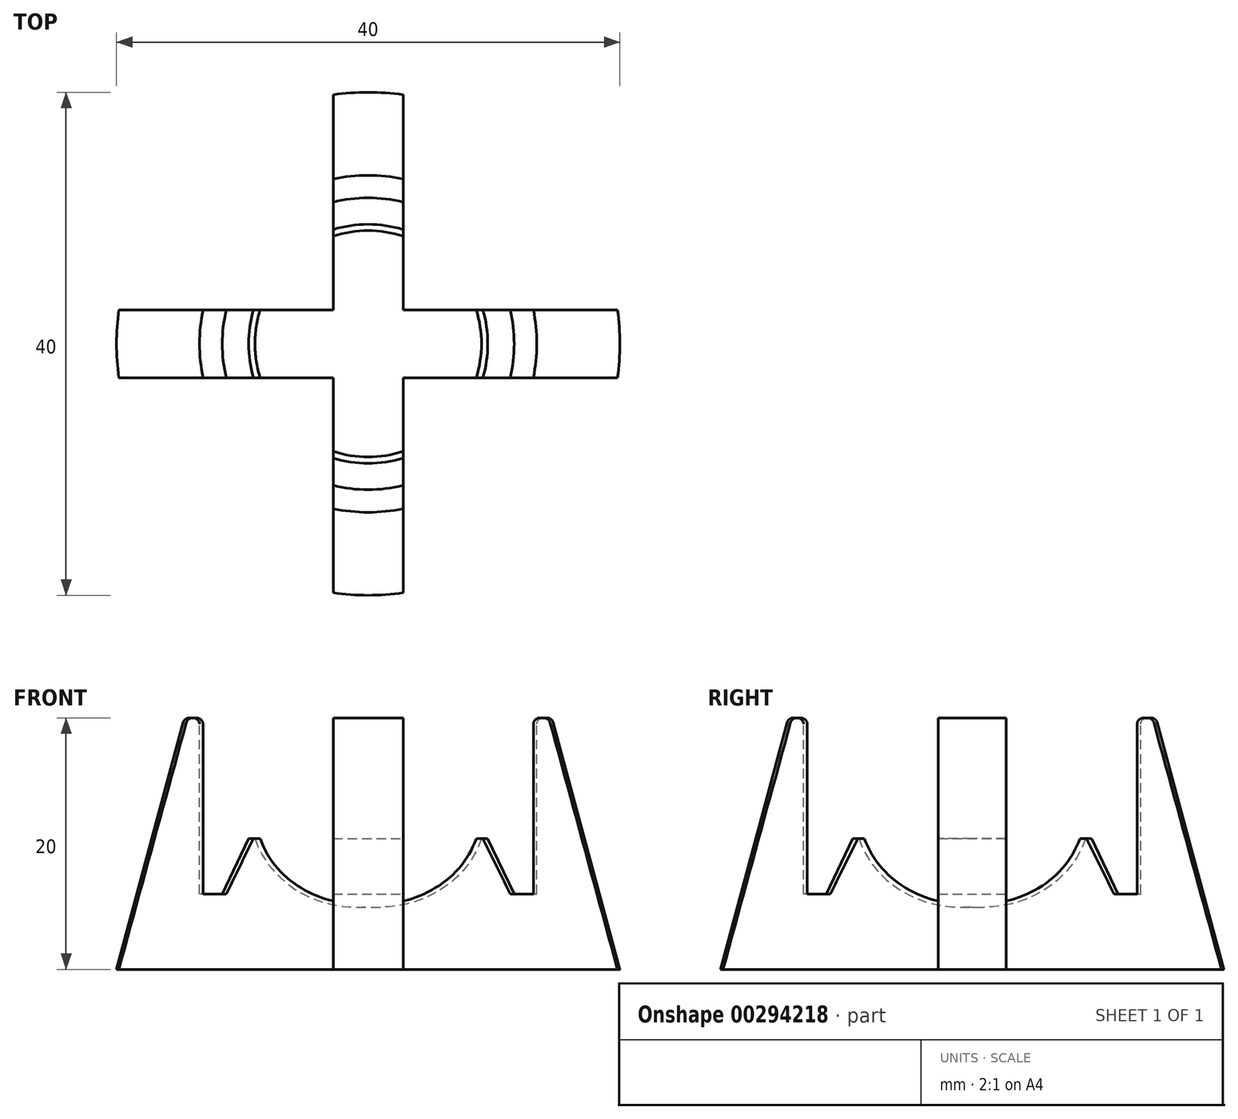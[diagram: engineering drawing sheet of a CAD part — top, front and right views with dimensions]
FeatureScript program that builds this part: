
annotation { "Feature Type Name" : "Feature", "Feature Type Description" : "" }
export const myFeature = defineFeature(function(context is Context, id is Id, definition is map)
    precondition{}
    {
        {
            var Q0;
            Q0=qCreatedBy(makeId("Front.planeOp"),FACE);
            var sketch = newSketch(context, id + "F0", { "sketchPlane" : qUnion([Q0])});
            skLineSegment(sketch, "E0", {"start": v(0, 0) * mm, "end": v(-20, 0) * mm});
            skLineSegment(sketch, "E1", {"start": v(-20, 0) * mm, "end": v(-14.6, 20) * mm});
            skLineSegment(sketch, "E2", {"start": v(-14.6, 20) * mm, "end": v(-13.4, 20) * mm});
            skLineSegment(sketch, "E3", {"start": v(-13.4, 20) * mm, "end": v(-13.4, 20) * mm});
            skLineSegment(sketch, "E4", {"start": v(0, 5) * mm, "end": v(0, 0) * mm});
            skPoint(sketch, "E5", {"position": v(-9.5, 10.4) * mm});
            skLineSegment(sketch, "E6", {"start": v(-9.5, 10.4) * mm, "end": v(-11.6, 6) * mm});
            skLineSegment(sketch, "E7", {"start": v(-13.4, 20) * mm, "end": v(-13.4, 6) * mm});
            skLineSegment(sketch, "E8", {"start": v(-13.4, 6) * mm, "end": v(-11.6, 6) * mm});
            skLineSegment(sketch, "E9", {"start": v(-9.5, 10.4) * mm, "end": v(-9, 10.4) * mm});
            skEllipticalArc(sketch, "E10", {});
            skPoint(sketch, "E11", {"position": v(-13.4, 12.7) * mm});
            const initialGuessF0  = {"E10": [-0.0009394245789034281, 0.012652029710676027, 0, -1, 0.0077, 0.00842914595487551, 5.0091991960001465, 0.11168157500112041]};
            skSetInitialGuess(sketch, initialGuessF0);
            skSolve(sketch);
        }
        {
            var Q0;
            Q0=makeQuery(id+"F0.imprint","IMPRINT",FACE,{"disambiguationData":[TD([[makeQuery(id+"F0.imprint","IMPRINT",EDGE,{"derivedFrom":sQuery(id+"F0.wireOp",EDGE,"E0")}),-1.0]])]});
            var Q1;
            Q1=sQuery(id+"F0.wireOp",EDGE,"E4");
            revolve(context, id + "F1", {"entities" : qUnion([Q0]), "axis" : qUnion([Q1]), "revolveType" : RevolveType.FULL});
        }
        {
            var Q0;
            Q0=makeQuery(id+"F1.opRevolve","SWEPT_EDGE",EDGE,{"disambiguationData":[OSD([sQuery(id+"F0.wireOp",EDGE,"E1"),sQuery(id+"F0.wireOp",EDGE,"E2")])]});
            var Q1;
            Q1=makeQuery(id+"F1.opRevolve","SWEPT_EDGE",EDGE,{"disambiguationData":[OSD([sQuery(id+"F0.wireOp",EDGE,"E2"),sQuery(id+"F0.wireOp",EDGE,"E7")])]});
            fillet(context, id + "F2", {"entities" : qUnion([Q0, Q1]), "radius" : .5 * mm, "tangentPropagation" : true, "allowEdgeOverflow" : false});
        }
        {
            var Q0;
            Q0=qCreatedBy(makeId("Top.planeOp"),FACE);
            var sketch = newSketch(context, id + "F3", { "sketchPlane" : qUnion([Q0])});
            skLineSegment(sketch, "E12.bottom", {"start": v(-2.78, 2.7) * mm, "end": v(-23.8, 2.7) * mm});
            skLineSegment(sketch, "E12.top", {"start": v(-2.78, 22.01) * mm, "end": v(-23.8, 22.01) * mm});
            skLineSegment(sketch, "E12.left", {"start": v(-2.78, 2.7) * mm, "end": v(-2.78, 22.01) * mm});
            skLineSegment(sketch, "E12.right", {"start": v(-23.8, 2.7) * mm, "end": v(-23.8, 22.01) * mm});
            skLineSegment(sketch, "E13.MirrorCS", {"start": v(2.78, 2.7) * mm, "end": v(23.8, 2.7) * mm});
            skLineSegment(sketch, "E14.MirrorCS", {"start": v(23.8, 2.7) * mm, "end": v(23.8, 22.01) * mm});
            skLineSegment(sketch, "E15.MirrorCS", {"start": v(2.78, 22.01) * mm, "end": v(23.8, 22.01) * mm});
            skLineSegment(sketch, "E16.MirrorCS", {"start": v(2.78, 2.7) * mm, "end": v(2.78, 22.01) * mm});
            skLineSegment(sketch, "E17.MirrorCS", {"start": v(-2.78, -2.7) * mm, "end": v(-23.8, -2.7) * mm});
            skLineSegment(sketch, "E18.MirrorCS", {"start": v(-2.78, -2.7) * mm, "end": v(-2.78, -22.01) * mm});
            skLineSegment(sketch, "E19.MirrorCS", {"start": v(-2.78, -22.01) * mm, "end": v(-23.8, -22.01) * mm});
            skLineSegment(sketch, "E20.MirrorCS", {"start": v(-23.8, -2.7) * mm, "end": v(-23.8, -22.01) * mm});
            skLineSegment(sketch, "E21.MirrorCS", {"start": v(2.78, -2.7) * mm, "end": v(2.78, -22.01) * mm});
            skLineSegment(sketch, "E22.MirrorCS", {"start": v(23.8, -2.7) * mm, "end": v(23.8, -22.01) * mm});
            skLineSegment(sketch, "E23.MirrorCS", {"start": v(2.78, -2.7) * mm, "end": v(23.8, -2.7) * mm});
            skLineSegment(sketch, "E24.MirrorCS", {"start": v(2.78, -22.01) * mm, "end": v(23.8, -22.01) * mm});
            skSolve(sketch);
        }
        {
            var Q0;
            Q0 = qSketchRegion(id + "F3", true);
            extrude(context, id + "F4", {"entities" : qUnion([Q0]), "operationType" : NewBodyOperationType.REMOVE, "depth" : 25 * mm});
        }
    });
